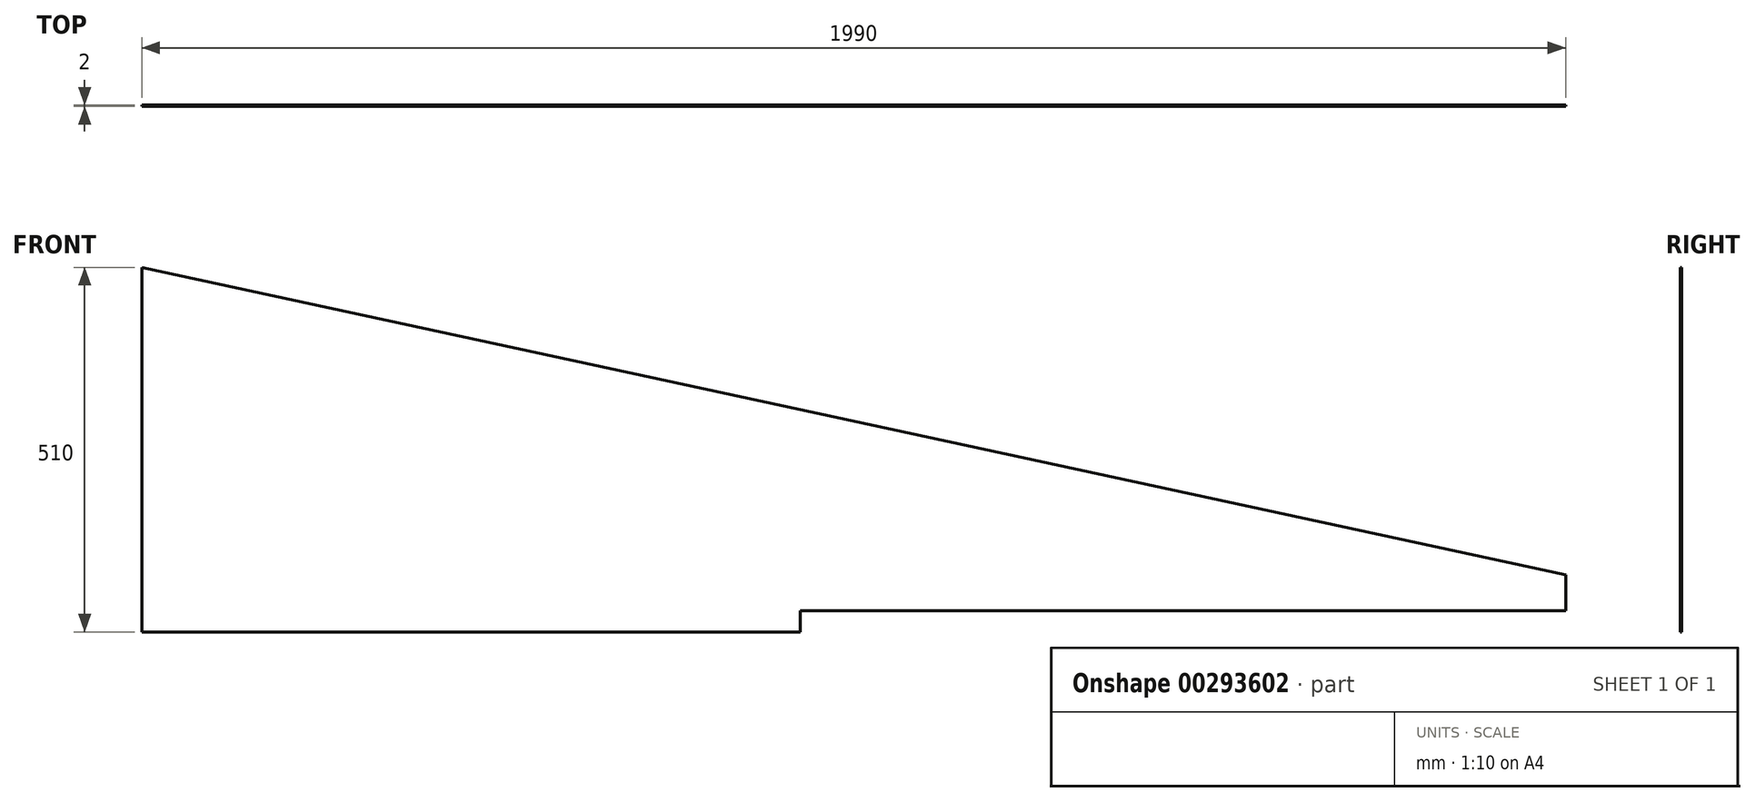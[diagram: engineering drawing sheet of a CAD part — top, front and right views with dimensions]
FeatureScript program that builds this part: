
annotation { "Feature Type Name" : "Feature", "Feature Type Description" : "" }
export const myFeature = defineFeature(function(context is Context, id is Id, definition is map)
    precondition{}
    {
        {
            var Q0;
            Q0=qCreatedBy(makeId("Front.planeOp"),FACE);
            var sketch = newSketch(context, id + "F0", { "sketchPlane" : qUnion([Q0])});
            skLineSegment(sketch, "E0.top", {"start": v(-995, -225) * mm, "end": v(995, -225) * mm, "construction": true});
            skLineSegment(sketch, "E0.left", {"start": v(-995, 225) * mm, "end": v(-995, -225) * mm});
            skLineSegment(sketch, "E0.right", {"start": v(995, -205) * mm, "end": v(995, -225) * mm});
            skPoint(sketch, "E0.middle", {"position": v(0, 0) * mm});
            skLineSegment(sketch, "E1", {"start": v(-995, 225) * mm, "end": v(995, -205) * mm});
            skPoint(sketch, "E2.orphan", {"position": v(995, 225) * mm});
            skLineSegment(sketch, "E3", {"start": v(-995, -225) * mm, "end": v(-995, -285) * mm});
            skLineSegment(sketch, "E4", {"start": v(-995, -285) * mm, "end": v(-75, -285) * mm});
            skLineSegment(sketch, "E5", {"start": v(-75, -285) * mm, "end": v(-75, -255) * mm});
            skLineSegment(sketch, "E6", {"start": v(-75, -255) * mm, "end": v(995, -255) * mm});
            skLineSegment(sketch, "E7", {"start": v(995, -225) * mm, "end": v(995, -255) * mm});
            skSolve(sketch);
        }
        {
            var Q0;
            Q0=makeQuery(id+"F0.imprint","IMPRINT",FACE,{"disambiguationData":[TD([[makeQuery(id+"F0.imprint","IMPRINT",EDGE,{"derivedFrom":sQuery(id+"F0.wireOp",EDGE,"E0.top")}),1.0]])]});
            var Q1;
            Q1=makeQuery(id+"F0.imprint","IMPRINT",FACE,{"disambiguationData":[TD([[makeQuery(id+"F0.imprint","IMPRINT",EDGE,{"derivedFrom":sQuery(id+"F0.wireOp",EDGE,"E0.left")}),1.0]])]});
            extrude(context, id + "F1", {"entities" : qUnion([Q0, Q1]), "depth" : 2 * mm});
        }
    });
